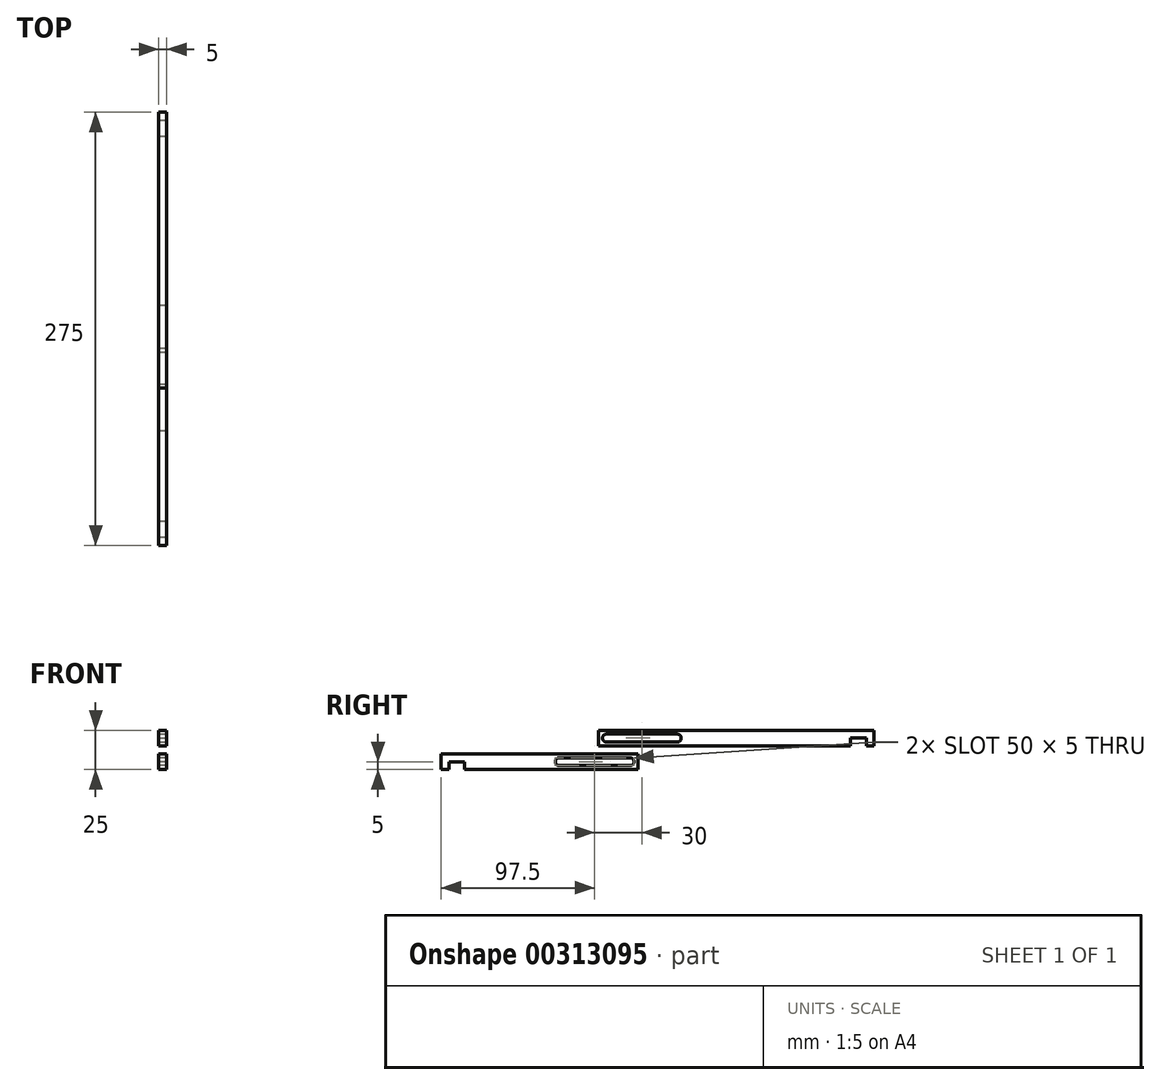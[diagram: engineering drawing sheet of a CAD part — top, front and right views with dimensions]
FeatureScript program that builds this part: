
annotation { "Feature Type Name" : "Feature", "Feature Type Description" : "" }
export const myFeature = defineFeature(function(context is Context, id is Id, definition is map)
    precondition{}
    {
        {
            var Q0;
            Q0=qCreatedBy(makeId("Right.planeOp"),FACE);
            var sketch = newSketch(context, id + "F0", { "sketchPlane" : qUnion([Q0])});
            skLineSegment(sketch, "E0", {"start": v(125, 0) * mm, "end": v(125, 10) * mm});
            skLineSegment(sketch, "E1", {"start": v(0, 0) * mm, "end": v(5, 0) * mm});
            skLineSegment(sketch, "E2", {"start": v(5, 0) * mm, "end": v(5, 5) * mm});
            skLineSegment(sketch, "E3", {"start": v(5, 5) * mm, "end": v(15, 5) * mm});
            skLineSegment(sketch, "E4", {"start": v(15, 5) * mm, "end": v(15, 0) * mm});
            skLineSegment(sketch, "E5", {"start": v(15, 0) * mm, "end": v(125, 0) * mm});
            skLineSegment(sketch, "E6", {"start": v(125, 10) * mm, "end": v(0, 10) * mm});
            skLineSegment(sketch, "E7", {"start": v(0, 10) * mm, "end": v(0, 0) * mm});
            skLineSegment(sketch, "E8", {"start": v(125, 5) * mm, "end": v(120, 5) * mm, "construction": true});
            skLineSegment(sketch, "E9", {"start": v(120, 5) * mm, "end": v(120, 10) * mm, "construction": true});
            skArc(sketch, "E10", {"start": v(120, 2.5) * mm, "mid": v(122.5, 5) * mm, "end": v(120, 7.5) * mm});
            skLineSegment(sketch, "E11", {"start": v(120, 5) * mm, "end": v(105, 5) * mm, "construction": true});
            skLineSegment(sketch, "E12", {"start": v(105, 5) * mm, "end": v(90, 5) * mm, "construction": true});
            skLineSegment(sketch, "E13", {"start": v(90, 5) * mm, "end": v(75, 5) * mm, "construction": true});
            skArc(sketch, "E14", {"start": v(75, 7.5) * mm, "mid": v(72.5, 5) * mm, "end": v(75, 2.5) * mm});
            skLineSegment(sketch, "E15", {"start": v(75, 7.5) * mm, "end": v(120, 7.5) * mm});
            skLineSegment(sketch, "E16", {"start": v(75, 2.5) * mm, "end": v(120, 2.5) * mm});
            skSolve(sketch);
        }
        {
            var Q0;
            Q0=makeQuery(id+"F0.imprint","IMPRINT",FACE,{"disambiguationData":[TD([[makeQuery(id+"F0.imprint","IMPRINT",EDGE,{"derivedFrom":sQuery(id+"F0.wireOp",EDGE,"E0")}),1.0]])]});
            extrude(context, id + "F1", {"entities" : qUnion([Q0]), "depth" : 5 * mm});
        }
        {
            var Q0;
            Q0=makeQuery(id+"F1.opExtrude","CAP_FACE",FACE,{"disambiguationData":[OSD([sQuery(id+"F0.wireOp",EDGE,"E0"),sQuery(id+"F0.wireOp",EDGE,"E1"),sQuery(id+"F0.wireOp",EDGE,"E2"),sQuery(id+"F0.wireOp",EDGE,"E3"),sQuery(id+"F0.wireOp",EDGE,"E4"),sQuery(id+"F0.wireOp",EDGE,"E5"),sQuery(id+"F0.wireOp",EDGE,"E6"),sQuery(id+"F0.wireOp",EDGE,"E7"),sQuery(id+"F0.wireOp",EDGE,"E10")])],"isStart":false});
            var sketch = newSketch(context, id + "F2", { "sketchPlane" : qUnion([Q0])});
            skLineSegment(sketch, "E17", {"start": v(15, 0) * mm, "end": v(260, 0) * mm, "construction": true});
            skLineSegment(sketch, "E18", {"start": v(260, 0) * mm, "end": v(260, 15) * mm, "construction": true});
            skLineSegment(sketch, "E19", {"start": v(260, 15) * mm, "end": v(260, 20) * mm});
            skLineSegment(sketch, "E20", {"start": v(260, 20) * mm, "end": v(270, 20) * mm});
            skLineSegment(sketch, "E21", {"start": v(270, 20) * mm, "end": v(270, 15) * mm});
            skLineSegment(sketch, "E22", {"start": v(270, 15) * mm, "end": v(275, 15) * mm});
            skLineSegment(sketch, "E23", {"start": v(275, 15) * mm, "end": v(275, 25) * mm});
            skLineSegment(sketch, "E24", {"start": v(275, 25) * mm, "end": v(100, 25) * mm});
            skLineSegment(sketch, "E25", {"start": v(100, 25) * mm, "end": v(100, 0) * mm, "construction": true});
            skLineSegment(sketch, "E26", {"start": v(100, 25) * mm, "end": v(100, 15) * mm});
            skLineSegment(sketch, "E27", {"start": v(100, 15) * mm, "end": v(260, 15) * mm});
            skPoint(sketch, "E28.endSnap0", {"position": v(100, 20) * mm});
            skLineSegment(sketch, "E29", {"start": v(105, 20) * mm, "end": v(120, 20) * mm, "construction": true});
            skLineSegment(sketch, "E30", {"start": v(120, 20) * mm, "end": v(120, 5) * mm, "construction": true});
            skArc(sketch, "E31", {"start": v(105, 22.5) * mm, "mid": v(102.5, 20) * mm, "end": v(105, 17.5) * mm});
            skLineSegment(sketch, "E32", {"start": v(120, 20) * mm, "end": v(135, 20) * mm, "construction": true});
            skLineSegment(sketch, "E33", {"start": v(135, 20) * mm, "end": v(150, 20) * mm, "construction": true});
            skArc(sketch, "E34", {"start": v(150, 17.5) * mm, "mid": v(152.5, 20) * mm, "end": v(150, 22.5) * mm});
            skLineSegment(sketch, "E35", {"start": v(105, 20) * mm, "end": v(100, 20) * mm, "construction": true});
            skLineSegment(sketch, "E36", {"start": v(105, 22.5) * mm, "end": v(150, 22.5) * mm});
            skLineSegment(sketch, "E37", {"start": v(105, 17.5) * mm, "end": v(150, 17.5) * mm});
            skSolve(sketch);
        }
        {
            var Q0;
            Q0 = qSketchRegion(id + "F2", true);
            extrude(context, id + "F3", {"entities" : qUnion([Q0]), "oppositeDirection" : true, "depth" : 5 * mm});
        }
    });
